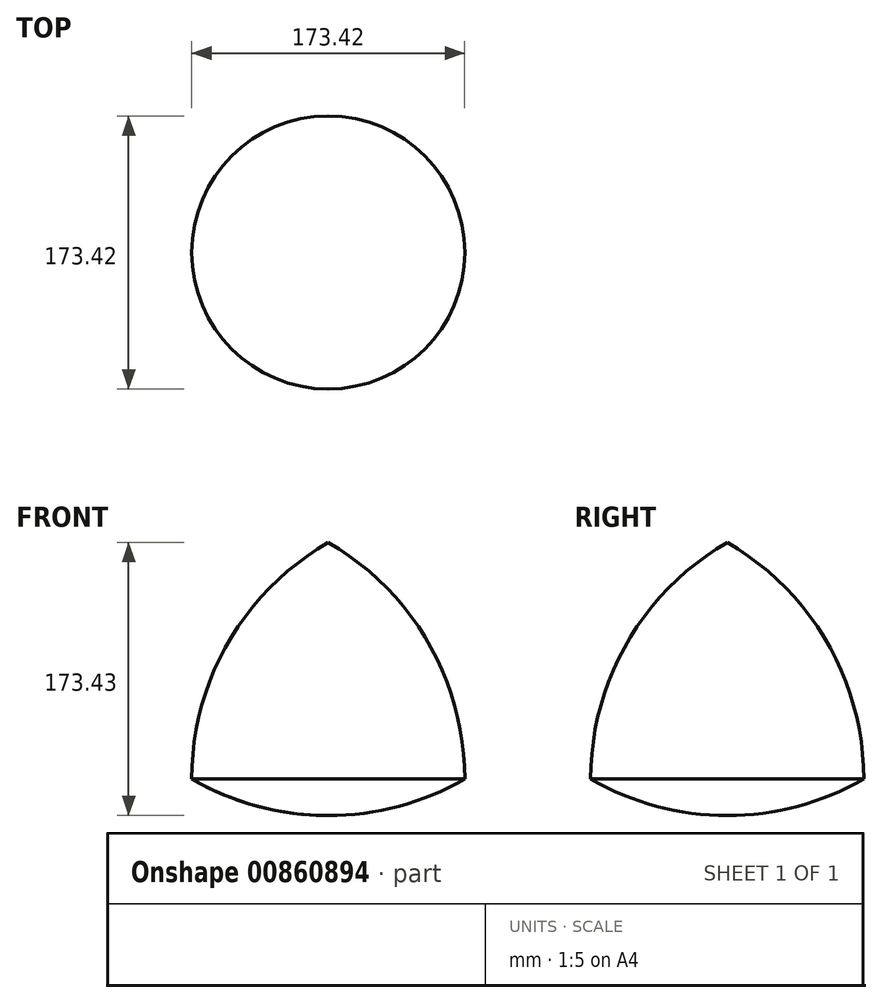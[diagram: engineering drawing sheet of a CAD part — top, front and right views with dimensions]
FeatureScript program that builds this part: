
annotation { "Feature Type Name" : "Feature", "Feature Type Description" : "" }
export const myFeature = defineFeature(function(context is Context, id is Id, definition is map)
    precondition{}
    {
        {
            var Q0;
            Q0=qCreatedBy(makeId("Front.planeOp"),FACE);
            var sketch = newSketch(context, id + "F0", { "sketchPlane" : qUnion([Q0])});
            skPoint(sketch, "E0.0.midPoint", {"position": v(0, -73.3) * mm});
            skCircle(sketch, "E1", {"center": v(0, 100.13) * mm, "radius": 173.42 * mm});
            skCircle(sketch, "E2", {"center": v(86.71, -50.06) * mm, "radius": 173.42 * mm});
            skCircle(sketch, "E3", {"center": v(-86.71, -50.06) * mm, "radius": 173.42 * mm});
            skLineSegment(sketch, "E4", {"start": v(0, 100.13) * mm, "end": v(0, -73.3) * mm});
            skSolve(sketch);
        }
        {
            var Q0;
            {var subQ0=sQuery(id+"F0.wireOp",EDGE,"E4");Q0=makeQuery(id+"F0.imprint","IMPRINT",FACE,{"disambiguationData":[TD([[makeQuery(id+"F0.imprint","IMPRINT",EDGE,{"derivedFrom":subQ0}),1.0]])]});}
            var Q1;
            Q1=sQuery(id+"F0.wireOp",EDGE,"E4");
            revolve(context, id + "F1", {"surfaceOperationType" : NewSurfaceOperationType.NEW, "entities" : qUnion([Q0]), "axis" : qUnion([Q1]), "revolveType" : RevolveType.FULL});
        }
    });
